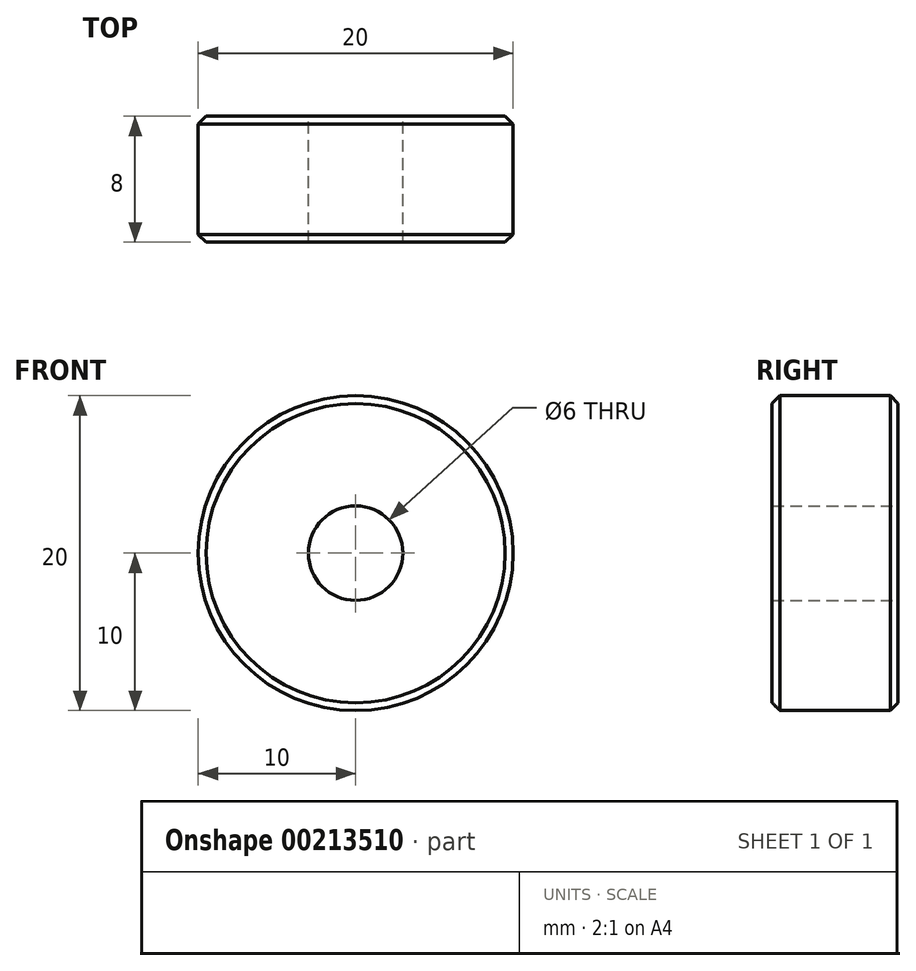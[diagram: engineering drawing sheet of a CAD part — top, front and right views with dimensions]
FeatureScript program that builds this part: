
annotation { "Feature Type Name" : "Feature", "Feature Type Description" : "" }
export const myFeature = defineFeature(function(context is Context, id is Id, definition is map)
    precondition{}
    {
        {
            var Q0;
            Q0=qCreatedBy(makeId("Front.planeOp"),FACE);
            var sketch = newSketch(context, id + "F0", { "sketchPlane" : qUnion([Q0])});
            skCircle(sketch, "E0", {"center": v(0, 0) * mm, "radius": 10 * mm});
            skCircle(sketch, "E1", {"center": v(0, 0) * mm, "radius": 3 * mm});
            skSolve(sketch);
        }
        {
            var Q0;
            Q0 = qSketchRegion(id + "F0", true);
            extrude(context, id + "F1", {"entities" : qUnion([Q0]), "depth" : 8 * mm});
        }
        {
            var Q0;
            Q0=makeQuery(id+"F1.opExtrude","CAP_EDGE",EDGE,{"disambiguationData":[OSD([sQuery(id+"F0.wireOp",EDGE,"E0")])],"isStart":false});
            var Q1;
            Q1=makeQuery(id+"F1.opExtrude","CAP_EDGE",EDGE,{"disambiguationData":[OSD([sQuery(id+"F0.wireOp",EDGE,"E0")])],"isStart":true});
            chamfer(context, id + "F2", {"entities" : qUnion([Q0, Q1]), "width" : 0.5 * mm, "tangentPropagation" : true});
        }
    });
